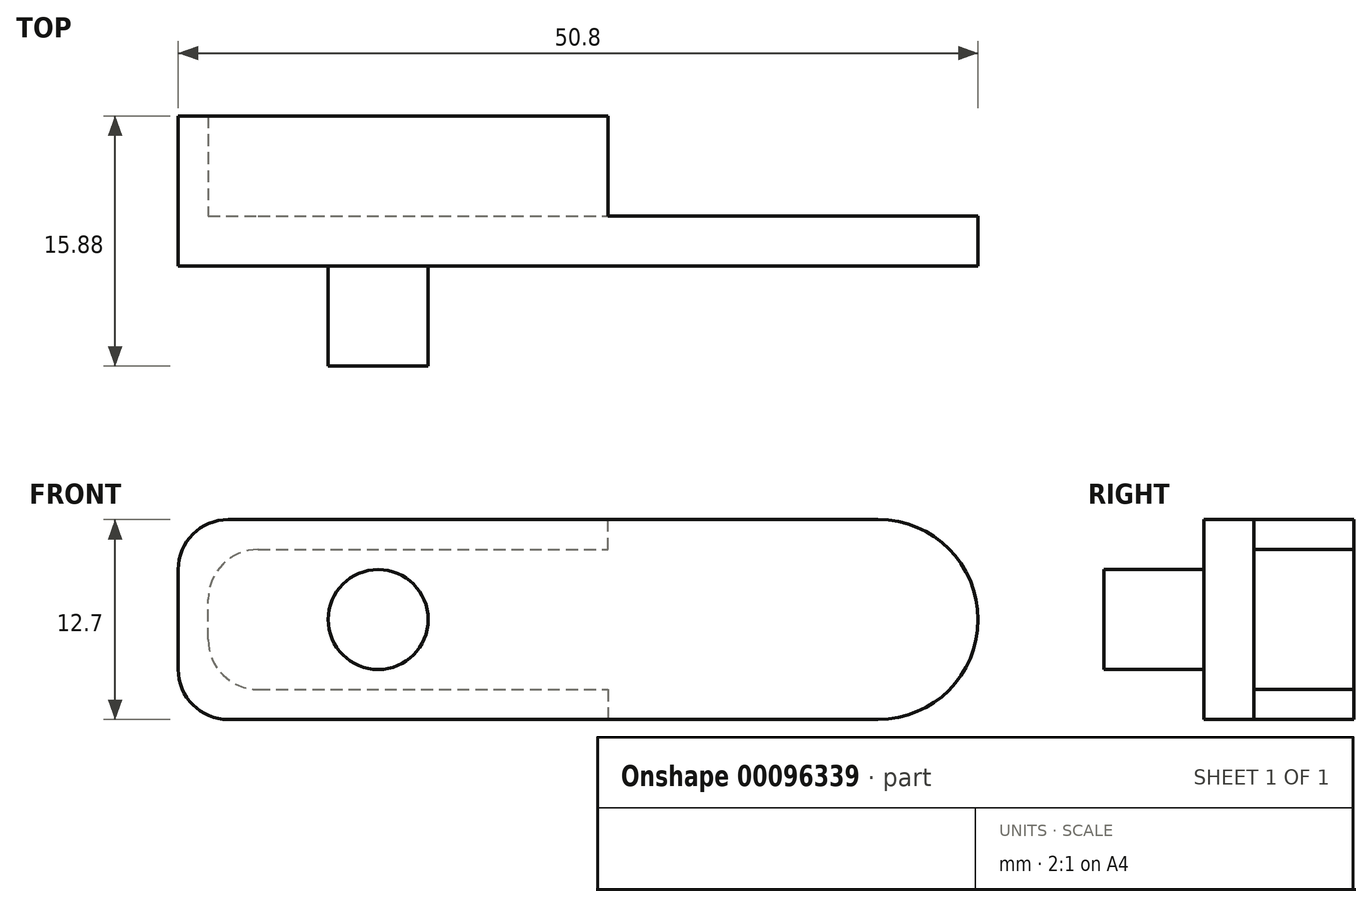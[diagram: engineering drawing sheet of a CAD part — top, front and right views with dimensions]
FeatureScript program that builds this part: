
annotation { "Feature Type Name" : "Feature", "Feature Type Description" : "" }
export const myFeature = defineFeature(function(context is Context, id is Id, definition is map)
    precondition{}
    {
        {
            var Q0;
            Q0=qCreatedBy(makeId("Front.planeOp"),FACE);
            var sketch = newSketch(context, id + "F0", { "sketchPlane" : qUnion([Q0])});
            skLineSegment(sketch, "E0.bottom", {"start": v(-10.39, 4.92) * mm, "end": v(40.41, 4.92) * mm});
            skLineSegment(sketch, "E0.top", {"start": v(-10.39, -7.78) * mm, "end": v(40.41, -7.78) * mm});
            skLineSegment(sketch, "E0.left", {"start": v(-10.39, 4.92) * mm, "end": v(-10.39, -7.78) * mm});
            skLineSegment(sketch, "E0.right", {"start": v(40.41, 4.92) * mm, "end": v(40.41, -7.78) * mm});
            skSolve(sketch);
        }
        {
            var Q0;
            Q0 = qSketchRegion(id + "F0", true);
            extrude(context, id + "F1", {"entities" : qUnion([Q0]), "depth" : 3.17 * mm});
        }
        {
            var Q0;
            Q0=makeQuery(id+"F1.opExtrude","CAP_FACE",FACE,{"disambiguationData":[OSD([sQuery(id+"F0.wireOp",EDGE,"E0.bottom"),sQuery(id+"F0.wireOp",EDGE,"E0.top"),sQuery(id+"F0.wireOp",EDGE,"E0.left"),sQuery(id+"F0.wireOp",EDGE,"E0.right")])],"isStart":false});
            var sketch = newSketch(context, id + "F2", { "sketchPlane" : qUnion([Q0])});
            skCircle(sketch, "E1", {"center": v(2.31, -1.43) * mm, "radius": 3.18 * mm});
            skPoint(sketch, "E1.centerSnap0", {"position": v(-10.39, -1.43) * mm});
            skSolve(sketch);
        }
        {
            var Q0;
            Q0 = qSketchRegion(id + "F2", true);
            extrude(context, id + "F3", {"entities" : qUnion([Q0]), "operationType" : NewBodyOperationType.ADD, "depth" : 6.35 * mm});
        }
        {
            var Q0;
            Q0=makeQuery(id+"F1.opExtrude","CAP_FACE",FACE,{"disambiguationData":[OSD([sQuery(id+"F0.wireOp",EDGE,"E0.bottom"),sQuery(id+"F0.wireOp",EDGE,"E0.top"),sQuery(id+"F0.wireOp",EDGE,"E0.left"),sQuery(id+"F0.wireOp",EDGE,"E0.right")])],"isStart":true});
            var sketch = newSketch(context, id + "F4", { "sketchPlane" : qUnion([Q0])});
            skLineSegment(sketch, "E2", {"start": v(8.48, -5.88) * mm, "end": v(-16.92, -5.88) * mm});
            skLineSegment(sketch, "E3", {"start": v(-16.92, -5.88) * mm, "end": v(-16.92, -7.78) * mm});
            skLineSegment(sketch, "E4", {"start": v(8.48, -5.88) * mm, "end": v(8.48, 3.01) * mm});
            skLineSegment(sketch, "E5", {"start": v(8.48, 3.01) * mm, "end": v(-16.92, 3.01) * mm});
            skLineSegment(sketch, "E6", {"start": v(-16.92, 3.01) * mm, "end": v(-16.92, 4.92) * mm});
            skSolve(sketch);
        }
        {
            var Q0;
            Q0=makeQuery(id+"F4.imprint","IMPRINT",FACE,{"disambiguationData":[TD([[makeQuery(id+"F4.imprint","IMPRINT",EDGE,{"derivedFrom":sQuery(id+"F4.wireOp",EDGE,"E2")}),1.0]])]});
            extrude(context, id + "F5", {"entities" : qUnion([Q0]), "operationType" : NewBodyOperationType.ADD, "depth" : 6.35 * mm});
        }
        {
            var Q0;
            Q0=makeQuery(id+"F1.opExtrude","SWEPT_EDGE",EDGE,{"disambiguationData":[OSD([sQuery(id+"F0.wireOp",EDGE,"E0.bottom"),sQuery(id+"F0.wireOp",EDGE,"E0.right")])]});
            var Q1;
            Q1=makeQuery(id+"F1.opExtrude","SWEPT_EDGE",EDGE,{"disambiguationData":[OSD([sQuery(id+"F0.wireOp",EDGE,"E0.top"),sQuery(id+"F0.wireOp",EDGE,"E0.right")])]});
            fillet(context, id + "F6", {"entities" : qUnion([Q0, Q1]), "radius" : 6.35 * mm, "tangentPropagation" : true, "allowEdgeOverflow" : false});
        }
        {
            var Q0;
            Q0=makeQuery(id+"F5.opExtrude","SWEPT_EDGE",EDGE,{"disambiguationData":[OSD([sQuery(id+"F4.wireOp",EDGE,"E4"),sQuery(id+"F4.wireOp",EDGE,"E5")])]});
            var Q1;
            Q1=makeQuery(id+"F5.opExtrude","SWEPT_EDGE",EDGE,{"disambiguationData":[OSD([sQuery(id+"F4.wireOp",EDGE,"E2"),sQuery(id+"F4.wireOp",EDGE,"E4")])]});
            var Q2;
            {var subQ0=sQuery(id+"F0.wireOp",EDGE,"E0.left");var subQ1=sQuery(id+"F0.wireOp",EDGE,"E0.bottom");Q2=makeQuery(id+"F5.boolean.opBoolean","MERGE",EDGE,{"derivedFrom":[makeQuery(id+"F1.opExtrude","SWEPT_EDGE",EDGE,{"disambiguationData":[OSD([subQ1,subQ0])]}),makeQuery(id+"F5.opExtrude","SWEPT_EDGE",EDGE,{"disambiguationData":[OSD([subQ1,subQ0])]})]});}
            var Q3;
            {var subQ0=sQuery(id+"F0.wireOp",EDGE,"E0.left");var subQ1=sQuery(id+"F0.wireOp",EDGE,"E0.top");Q3=makeQuery(id+"F5.boolean.opBoolean","MERGE",EDGE,{"derivedFrom":[makeQuery(id+"F1.opExtrude","SWEPT_EDGE",EDGE,{"disambiguationData":[OSD([subQ1,subQ0])]}),makeQuery(id+"F5.opExtrude","SWEPT_EDGE",EDGE,{"disambiguationData":[OSD([subQ1,subQ0])]})]});}
            fillet(context, id + "F7", {"entities" : qUnion([Q0, Q1, Q2, Q3]), "radius" : 3.17 * mm, "tangentPropagation" : true, "allowEdgeOverflow" : false});
        }
    });
